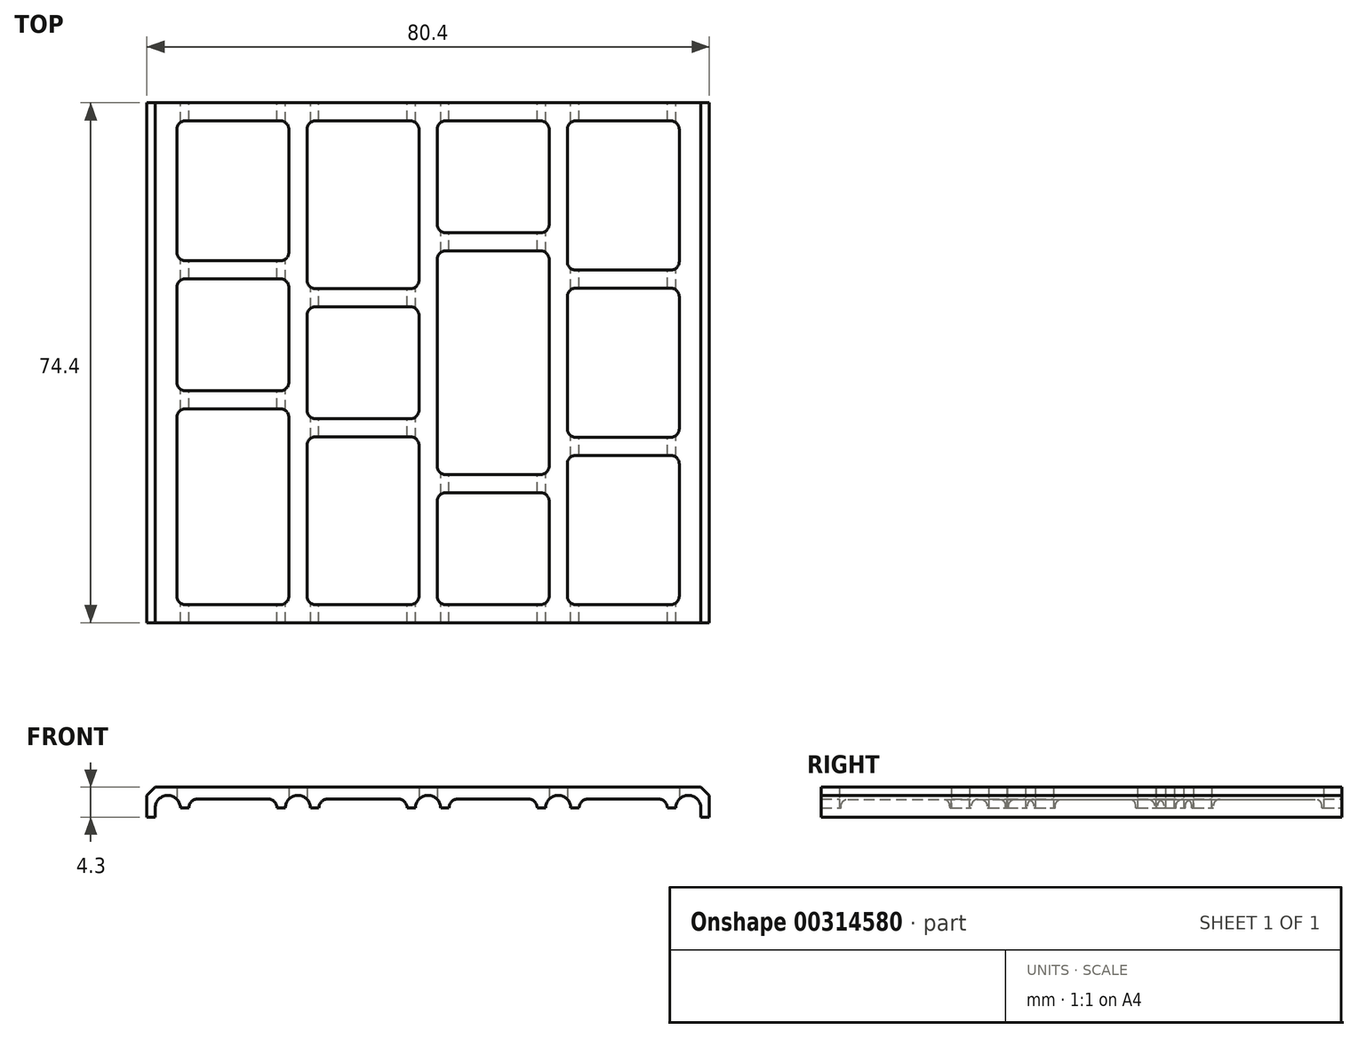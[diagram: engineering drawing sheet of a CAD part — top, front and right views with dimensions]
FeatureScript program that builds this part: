
annotation { "Feature Type Name" : "Feature", "Feature Type Description" : "" }
export const myFeature = defineFeature(function(context is Context, id is Id, definition is map)
    precondition{}
    {
        {
            var Q0;
            Q0=qCreatedBy(makeId("Front.planeOp"),FACE);
            var sketch = newSketch(context, id + "F0", { "sketchPlane" : qUnion([Q0])});
            skCircle(sketch, "E0", {"center": v(-37.2, -1.3) * mm, "radius": 1.3 * mm});
            skLineSegment(sketch, "E1", {"start": v(-37.2, -1.3) * mm, "end": v(-37.2, 0) * mm, "construction": true});
            skLineSegment(sketch, "E2", {"start": v(0, 0) * mm, "end": v(0, -7.18) * mm, "construction": true});
            skPoint(sketch, "E3", {"position": v(-38.5, -1.3) * mm});
            skCircle(sketch, "E4.1.0.0", {"center": v(-18.6, -1.3) * mm, "radius": 1.3 * mm});
            skCircle(sketch, "E4.2.0.0", {"center": v(0, -1.3) * mm, "radius": 1.3 * mm});
            skCircle(sketch, "E4.3.0.0", {"center": v(18.6, -1.3) * mm, "radius": 1.3 * mm});
            skCircle(sketch, "E4.4.0.0", {"center": v(37.2, -1.3) * mm, "radius": 1.3 * mm});
            skLineSegment(sketch, "E4.direction1", {"start": v(-37.2, -1.3) * mm, "end": v(-18.6, -1.3) * mm, "construction": true});
            skPoint(sketch, "E5", {"position": v(38.5, -1.3) * mm});
            skLineSegment(sketch, "E6", {"start": v(37.2, -1.3) * mm, "end": v(37.2, 0) * mm, "construction": true});
            skLineSegment(sketch, "E7", {"start": v(-37.2, 0) * mm, "end": v(37.2, 0) * mm, "construction": true});
            skPoint(sketch, "E8", {"position": v(-35.9, -1.3) * mm});
            skSolve(sketch);
        }
        {
            var Q0;
            Q0=qCreatedBy(makeId("Front.planeOp"),FACE);
            var sketch = newSketch(context, id + "F1", { "sketchPlane" : qUnion([Q0])});
            skArc(sketch, "E9", {"start": v(-35.4, -1.3) * mm, "mid": v(-37.2, 0.5) * mm, "end": v(-39, -1.3) * mm});
            skArc(sketch, "E10", {"start": v(-16.8, -1.3) * mm, "mid": v(-18.6, 0.5) * mm, "end": v(-20.4, -1.3) * mm});
            skArc(sketch, "E11", {"start": v(0, 0.5) * mm, "mid": v(-1.27, -0.03) * mm, "end": v(-1.8, -1.3) * mm});
            skLineSegment(sketch, "E12.trimOffspring", {"start": v(0, 0.5) * mm, "end": v(0, 1.7) * mm});
            skLineSegment(sketch, "E13.trimOffspring", {"start": v(-16.8, -1.3) * mm, "end": v(-15.6, -1.3) * mm});
            skLineSegment(sketch, "E14.trimOffspring", {"start": v(-35.4, -1.3) * mm, "end": v(-34.2, -1.3) * mm});
            skLineSegment(sketch, "E15", {"start": v(-39, -1.3) * mm, "end": v(-39, -2.6) * mm});
            skLineSegment(sketch, "E16", {"start": v(-39, -2.6) * mm, "end": v(-40.2, -2.6) * mm});
            skLineSegment(sketch, "E17", {"start": v(-40.2, -2.6) * mm, "end": v(-40.2, 1.7) * mm});
            skLineSegment(sketch, "E18", {"start": v(-40.2, 1.7) * mm, "end": v(0, 1.7) * mm});
            skPoint(sketch, "E19", {"position": v(0, -2.6) * mm});
            skLineSegment(sketch, "E20", {"start": v(-34.2, -1.3) * mm, "end": v(-34.2, 0) * mm});
            skLineSegment(sketch, "E21", {"start": v(-34.2, 0) * mm, "end": v(-21.6, 0) * mm});
            skLineSegment(sketch, "E22", {"start": v(-21.6, 0) * mm, "end": v(-21.6, -1.3) * mm});
            skLineSegment(sketch, "E23", {"start": v(-15.6, -1.3) * mm, "end": v(-15.6, 0) * mm});
            skLineSegment(sketch, "E24", {"start": v(-15.6, 0) * mm, "end": v(-3, 0) * mm});
            skLineSegment(sketch, "E25", {"start": v(-3, 0) * mm, "end": v(-3, -1.3) * mm});
            skLineSegment(sketch, "E26.trimOffspring", {"start": v(-21.6, -1.3) * mm, "end": v(-20.4, -1.3) * mm});
            skLineSegment(sketch, "E27.trimOffspring", {"start": v(-3, -1.3) * mm, "end": v(-1.8, -1.3) * mm});
            skSolve(sketch);
        }
        {
            var Q0;
            Q0 = qSketchRegion(id + "F1", true);
            extrude(context, id + "F2", {"entities" : qUnion([Q0]), "depth" : (77 - 5.2 + 2.6) * mm});
        }
        {
            var Q0;
            Q0=makeQuery(id+"F2.opExtrude","SWEPT_EDGE",EDGE,{"disambiguationData":[OSD([sQuery(id+"F1.wireOp",EDGE,"E20"),sQuery(id+"F1.wireOp",EDGE,"E21")])]});
            var Q1;
            Q1=makeQuery(id+"F2.opExtrude","SWEPT_EDGE",EDGE,{"disambiguationData":[OSD([sQuery(id+"F1.wireOp",EDGE,"E21"),sQuery(id+"F1.wireOp",EDGE,"E22")])]});
            var Q2;
            Q2=makeQuery(id+"F2.opExtrude","SWEPT_EDGE",EDGE,{"disambiguationData":[OSD([sQuery(id+"F1.wireOp",EDGE,"E23"),sQuery(id+"F1.wireOp",EDGE,"E24")])]});
            var Q3;
            Q3=makeQuery(id+"F2.opExtrude","SWEPT_EDGE",EDGE,{"disambiguationData":[OSD([sQuery(id+"F1.wireOp",EDGE,"E24"),sQuery(id+"F1.wireOp",EDGE,"E25")])]});
            fillet(context, id + "F3", {"entities" : qUnion([Q0, Q1, Q2, Q3]), "radius" : 1.3 * mm, "tangentPropagation" : true, "allowEdgeOverflow" : false});
        }
        {
            var Q0;
            Q0=makeQuery(id+"F2.opExtrude","SWEPT_EDGE",EDGE,{"disambiguationData":[OSD([sQuery(id+"F1.wireOp",EDGE,"E17"),sQuery(id+"F1.wireOp",EDGE,"E18")])]});
            chamfer(context, id + "F4", {"entities" : qUnion([Q0]), "width" : 1.2 * mm, "tangentPropagation" : true});
        }
        {
            var Q0;
            Q0=makeQuery(id+"F2.opExtrude","SWEPT_BODY",BODY,{"disambiguationData":[OSD([sQuery(id+"F1.wireOp",EDGE,"E9"),sQuery(id+"F1.wireOp",EDGE,"E10"),sQuery(id+"F1.wireOp",EDGE,"E11"),sQuery(id+"F1.wireOp",EDGE,"E12.trimOffspring"),sQuery(id+"F1.wireOp",EDGE,"E13.trimOffspring"),sQuery(id+"F1.wireOp",EDGE,"E14.trimOffspring"),sQuery(id+"F1.wireOp",EDGE,"E15"),sQuery(id+"F1.wireOp",EDGE,"E16"),sQuery(id+"F1.wireOp",EDGE,"E17"),sQuery(id+"F1.wireOp",EDGE,"E18"),sQuery(id+"F1.wireOp",EDGE,"E20"),sQuery(id+"F1.wireOp",EDGE,"E21"),sQuery(id+"F1.wireOp",EDGE,"E22"),sQuery(id+"F1.wireOp",EDGE,"E23"),sQuery(id+"F1.wireOp",EDGE,"E24"),sQuery(id+"F1.wireOp",EDGE,"E25"),sQuery(id+"F1.wireOp",EDGE,"E26.trimOffspring"),sQuery(id+"F1.wireOp",EDGE,"E27.trimOffspring")])]});
            var Q1;
            Q1=qCreatedBy(makeId("Right.planeOp"),FACE);
            mirror(context, id + "F5", {"operationType" : NewBodyOperationType.ADD, "entities" : qUnion([Q0]), "mirrorPlane" : qUnion([Q1])});
        }
        {
            var Q0;
            Q0=qCreatedBy(makeId("Top.planeOp"),FACE);
            var sketch = newSketch(context, id + "F6", { "sketchPlane" : qUnion([Q0])});
            skLineSegment(sketch, "E28.bottom", {"start": v(-35.9, -2.6) * mm, "end": v(-19.9, -2.6) * mm});
            skLineSegment(sketch, "E28.top", {"start": v(-35.9, -22.6) * mm, "end": v(-19.9, -22.6) * mm});
            skLineSegment(sketch, "E28.left", {"start": v(-35.9, -2.6) * mm, "end": v(-35.9, -22.6) * mm});
            skLineSegment(sketch, "E29", {"start": v(-19.9, -2.6) * mm, "end": v(-19.9, -22.6) * mm});
            skLineSegment(sketch, "E30.bottom", {"start": v(-35.9, -25.2) * mm, "end": v(-19.9, -25.2) * mm});
            skLineSegment(sketch, "E30.top", {"start": v(-35.9, -41.2) * mm, "end": v(-19.9, -41.2) * mm});
            skLineSegment(sketch, "E30.left", {"start": v(-35.9, -25.2) * mm, "end": v(-35.9, -41.2) * mm});
            skLineSegment(sketch, "E30.right", {"start": v(-19.9, -25.2) * mm, "end": v(-19.9, -41.2) * mm});
            skLineSegment(sketch, "E31.bottom", {"start": v(-35.9, -43.8) * mm, "end": v(-19.9, -43.8) * mm});
            skLineSegment(sketch, "E31.top", {"start": v(-35.9, -71.8) * mm, "end": v(-19.9, -71.8) * mm});
            skLineSegment(sketch, "E31.left", {"start": v(-35.9, -43.8) * mm, "end": v(-35.9, -71.8) * mm});
            skLineSegment(sketch, "E31.right", {"start": v(-19.9, -43.8) * mm, "end": v(-19.9, -71.8) * mm});
            skLineSegment(sketch, "E32.bottom", {"start": v(-17.3, -71.8) * mm, "end": v(-1.3, -71.8) * mm});
            skLineSegment(sketch, "E32.top", {"start": v(-17.3, -47.8) * mm, "end": v(-1.3, -47.8) * mm});
            skLineSegment(sketch, "E32.left", {"start": v(-17.3, -71.8) * mm, "end": v(-17.3, -47.8) * mm});
            skLineSegment(sketch, "E32.right", {"start": v(-1.3, -71.8) * mm, "end": v(-1.3, -47.8) * mm});
            skLineSegment(sketch, "E33.bottom", {"start": v(1.3, -71.8) * mm, "end": v(17.3, -71.8) * mm});
            skLineSegment(sketch, "E33.top", {"start": v(1.3, -55.8) * mm, "end": v(17.3, -55.8) * mm});
            skLineSegment(sketch, "E33.left", {"start": v(1.3, -71.8) * mm, "end": v(1.3, -55.8) * mm});
            skLineSegment(sketch, "E33.right", {"start": v(17.3, -71.8) * mm, "end": v(17.3, -55.8) * mm});
            skLineSegment(sketch, "E34.bottom", {"start": v(-17.3, -45.2) * mm, "end": v(-1.3, -45.2) * mm});
            skLineSegment(sketch, "E34.top", {"start": v(-17.3, -29.2) * mm, "end": v(-1.3, -29.2) * mm});
            skLineSegment(sketch, "E34.left", {"start": v(-17.3, -45.2) * mm, "end": v(-17.3, -29.2) * mm});
            skLineSegment(sketch, "E34.right", {"start": v(-1.3, -45.2) * mm, "end": v(-1.3, -29.2) * mm});
            skLineSegment(sketch, "E35.bottom", {"start": v(-17.3, -26.6) * mm, "end": v(-1.3, -26.6) * mm});
            skLineSegment(sketch, "E35.top", {"start": v(-17.3, -2.6) * mm, "end": v(-1.3, -2.6) * mm});
            skLineSegment(sketch, "E35.left", {"start": v(-17.3, -26.6) * mm, "end": v(-17.3, -2.6) * mm});
            skLineSegment(sketch, "E35.right", {"start": v(-1.3, -26.6) * mm, "end": v(-1.3, -2.6) * mm});
            skLineSegment(sketch, "E36.bottom", {"start": v(1.3, -2.6) * mm, "end": v(17.3, -2.6) * mm});
            skLineSegment(sketch, "E36.top", {"start": v(1.3, -18.6) * mm, "end": v(17.3, -18.6) * mm});
            skLineSegment(sketch, "E36.left", {"start": v(1.3, -2.6) * mm, "end": v(1.3, -18.6) * mm});
            skLineSegment(sketch, "E36.right", {"start": v(17.3, -2.6) * mm, "end": v(17.3, -18.6) * mm});
            skLineSegment(sketch, "E37.bottom", {"start": v(1.3, -21.2) * mm, "end": v(17.3, -21.2) * mm});
            skLineSegment(sketch, "E37.top", {"start": v(1.3, -53.2) * mm, "end": v(17.3, -53.2) * mm});
            skLineSegment(sketch, "E37.left", {"start": v(1.3, -21.2) * mm, "end": v(1.3, -53.2) * mm});
            skLineSegment(sketch, "E37.right", {"start": v(17.3, -21.2) * mm, "end": v(17.3, -53.2) * mm});
            skLineSegment(sketch, "E38.bottom", {"start": v(19.9, -2.6) * mm, "end": v(35.9, -2.6) * mm});
            skLineSegment(sketch, "E38.top", {"start": v(19.9, -71.8) * mm, "end": v(35.9, -71.8) * mm});
            skLineSegment(sketch, "E38.left", {"start": v(19.9, -2.6) * mm, "end": v(19.9, -23.93) * mm});
            skLineSegment(sketch, "E38.right", {"start": v(35.9, -2.6) * mm, "end": v(35.9, -23.93) * mm});
            skLineSegment(sketch, "E39", {"start": v(19.9, -23.93) * mm, "end": v(35.9, -23.93) * mm});
            skLineSegment(sketch, "E40", {"start": v(19.9, -26.53) * mm, "end": v(35.9, -26.53) * mm});
            skLineSegment(sketch, "E41.trimOffspring", {"start": v(19.9, -26.53) * mm, "end": v(19.9, -47.87) * mm});
            skLineSegment(sketch, "E42.trimOffspring", {"start": v(35.9, -26.53) * mm, "end": v(35.9, -47.87) * mm});
            skLineSegment(sketch, "E43", {"start": v(19.9, -47.87) * mm, "end": v(35.9, -47.87) * mm});
            skLineSegment(sketch, "E44", {"start": v(35.9, -50.47) * mm, "end": v(19.9, -50.47) * mm});
            skLineSegment(sketch, "E45.trimOffspring", {"start": v(19.9, -50.47) * mm, "end": v(19.9, -71.8) * mm});
            skLineSegment(sketch, "E46.trimOffspring", {"start": v(35.9, -50.47) * mm, "end": v(35.9, -71.8) * mm});
            skSolve(sketch);
        }
        {
            var Q0;
            Q0 = qSketchRegion(id + "F6", true);
            extrude(context, id + "F7", {"entities" : qUnion([Q0]), "operationType" : NewBodyOperationType.REMOVE, "endBound" : BoundingType.THROUGH_ALL, "depth" : 25 * mm, "hasSecondDirection" : true, "secondDirectionBound" : SecondDirectionBoundingType.THROUGH_ALL, "secondDirectionOppositeDirection" : true, "secondDirectionDepth" : 25 * mm});
        }
        {
            var Q0;
            Q0=makeQuery(id+"F7.boolean.opBoolean","COPY",EDGE,{"derivedFrom":makeQuery(id+"F7.opExtrude","SWEPT_EDGE",EDGE,{"disambiguationData":[OSD([sQuery(id+"F6.wireOp",EDGE,"E28.bottom"),sQuery(id+"F6.wireOp",EDGE,"E29")])]})});
            var Q1;
            Q1=makeQuery(id+"F7.boolean.opBoolean","COPY",EDGE,{"derivedFrom":makeQuery(id+"F7.opExtrude","SWEPT_EDGE",EDGE,{"disambiguationData":[OSD([sQuery(id+"F6.wireOp",EDGE,"E28.bottom"),sQuery(id+"F6.wireOp",EDGE,"E28.left")])]})});
            var Q2;
            Q2=makeQuery(id+"F7.boolean.opBoolean","COPY",EDGE,{"derivedFrom":makeQuery(id+"F7.opExtrude","SWEPT_EDGE",EDGE,{"disambiguationData":[OSD([sQuery(id+"F6.wireOp",EDGE,"E28.top"),sQuery(id+"F6.wireOp",EDGE,"E29")])]})});
            var Q3;
            Q3=makeQuery(id+"F7.boolean.opBoolean","COPY",EDGE,{"derivedFrom":makeQuery(id+"F7.opExtrude","SWEPT_EDGE",EDGE,{"disambiguationData":[OSD([sQuery(id+"F6.wireOp",EDGE,"E28.top"),sQuery(id+"F6.wireOp",EDGE,"E28.left")])]})});
            var Q4;
            Q4=makeQuery(id+"F7.boolean.opBoolean","COPY",EDGE,{"derivedFrom":makeQuery(id+"F7.opExtrude","SWEPT_EDGE",EDGE,{"disambiguationData":[OSD([sQuery(id+"F6.wireOp",EDGE,"E30.bottom"),sQuery(id+"F6.wireOp",EDGE,"E30.left")])]})});
            var Q5;
            Q5=makeQuery(id+"F7.boolean.opBoolean","COPY",EDGE,{"derivedFrom":makeQuery(id+"F7.opExtrude","SWEPT_EDGE",EDGE,{"disambiguationData":[OSD([sQuery(id+"F6.wireOp",EDGE,"E30.top"),sQuery(id+"F6.wireOp",EDGE,"E30.left")])]})});
            var Q6;
            Q6=makeQuery(id+"F7.boolean.opBoolean","COPY",EDGE,{"derivedFrom":makeQuery(id+"F7.opExtrude","SWEPT_EDGE",EDGE,{"disambiguationData":[OSD([sQuery(id+"F6.wireOp",EDGE,"E31.top"),sQuery(id+"F6.wireOp",EDGE,"E31.left")])]})});
            var Q7;
            Q7=makeQuery(id+"F7.boolean.opBoolean","COPY",EDGE,{"derivedFrom":makeQuery(id+"F7.opExtrude","SWEPT_EDGE",EDGE,{"disambiguationData":[OSD([sQuery(id+"F6.wireOp",EDGE,"E31.bottom"),sQuery(id+"F6.wireOp",EDGE,"E31.left")])]})});
            var Q8;
            Q8=makeQuery(id+"F7.boolean.opBoolean","COPY",EDGE,{"derivedFrom":makeQuery(id+"F7.opExtrude","SWEPT_EDGE",EDGE,{"disambiguationData":[OSD([sQuery(id+"F6.wireOp",EDGE,"E30.bottom"),sQuery(id+"F6.wireOp",EDGE,"E30.right")])]})});
            var Q9;
            Q9=makeQuery(id+"F7.boolean.opBoolean","COPY",EDGE,{"derivedFrom":makeQuery(id+"F7.opExtrude","SWEPT_EDGE",EDGE,{"disambiguationData":[OSD([sQuery(id+"F6.wireOp",EDGE,"E30.top"),sQuery(id+"F6.wireOp",EDGE,"E30.right")])]})});
            var Q10;
            Q10=makeQuery(id+"F7.boolean.opBoolean","COPY",EDGE,{"derivedFrom":makeQuery(id+"F7.opExtrude","SWEPT_EDGE",EDGE,{"disambiguationData":[OSD([sQuery(id+"F6.wireOp",EDGE,"E31.bottom"),sQuery(id+"F6.wireOp",EDGE,"E31.right")])]})});
            var Q11;
            Q11=makeQuery(id+"F7.boolean.opBoolean","COPY",EDGE,{"derivedFrom":makeQuery(id+"F7.opExtrude","SWEPT_EDGE",EDGE,{"disambiguationData":[OSD([sQuery(id+"F6.wireOp",EDGE,"E31.top"),sQuery(id+"F6.wireOp",EDGE,"E31.right")])]})});
            var Q12;
            Q12=makeQuery(id+"F7.boolean.opBoolean","COPY",EDGE,{"derivedFrom":makeQuery(id+"F7.opExtrude","SWEPT_EDGE",EDGE,{"disambiguationData":[OSD([sQuery(id+"F6.wireOp",EDGE,"E35.bottom"),sQuery(id+"F6.wireOp",EDGE,"E35.left")])]})});
            var Q13;
            Q13=makeQuery(id+"F7.boolean.opBoolean","COPY",EDGE,{"derivedFrom":makeQuery(id+"F7.opExtrude","SWEPT_EDGE",EDGE,{"disambiguationData":[OSD([sQuery(id+"F6.wireOp",EDGE,"E34.bottom"),sQuery(id+"F6.wireOp",EDGE,"E34.left")])]})});
            var Q14;
            Q14=makeQuery(id+"F7.boolean.opBoolean","COPY",EDGE,{"derivedFrom":makeQuery(id+"F7.opExtrude","SWEPT_EDGE",EDGE,{"disambiguationData":[OSD([sQuery(id+"F6.wireOp",EDGE,"E32.bottom"),sQuery(id+"F6.wireOp",EDGE,"E32.left")])]})});
            var Q15;
            Q15=makeQuery(id+"F7.boolean.opBoolean","COPY",EDGE,{"derivedFrom":makeQuery(id+"F7.opExtrude","SWEPT_EDGE",EDGE,{"disambiguationData":[OSD([sQuery(id+"F6.wireOp",EDGE,"E35.top"),sQuery(id+"F6.wireOp",EDGE,"E35.left")])]})});
            var Q16;
            Q16=makeQuery(id+"F7.boolean.opBoolean","COPY",EDGE,{"derivedFrom":makeQuery(id+"F7.opExtrude","SWEPT_EDGE",EDGE,{"disambiguationData":[OSD([sQuery(id+"F6.wireOp",EDGE,"E34.top"),sQuery(id+"F6.wireOp",EDGE,"E34.left")])]})});
            var Q17;
            Q17=makeQuery(id+"F7.boolean.opBoolean","COPY",EDGE,{"derivedFrom":makeQuery(id+"F7.opExtrude","SWEPT_EDGE",EDGE,{"disambiguationData":[OSD([sQuery(id+"F6.wireOp",EDGE,"E35.top"),sQuery(id+"F6.wireOp",EDGE,"E35.right")])]})});
            var Q18;
            Q18=makeQuery(id+"F7.boolean.opBoolean","COPY",EDGE,{"derivedFrom":makeQuery(id+"F7.opExtrude","SWEPT_EDGE",EDGE,{"disambiguationData":[OSD([sQuery(id+"F6.wireOp",EDGE,"E34.top"),sQuery(id+"F6.wireOp",EDGE,"E34.right")])]})});
            var Q19;
            Q19=makeQuery(id+"F7.boolean.opBoolean","COPY",EDGE,{"derivedFrom":makeQuery(id+"F7.opExtrude","SWEPT_EDGE",EDGE,{"disambiguationData":[OSD([sQuery(id+"F6.wireOp",EDGE,"E32.top"),sQuery(id+"F6.wireOp",EDGE,"E32.right")])]})});
            var Q20;
            Q20=makeQuery(id+"F7.boolean.opBoolean","COPY",EDGE,{"derivedFrom":makeQuery(id+"F7.opExtrude","SWEPT_EDGE",EDGE,{"disambiguationData":[OSD([sQuery(id+"F6.wireOp",EDGE,"E32.bottom"),sQuery(id+"F6.wireOp",EDGE,"E32.right")])]})});
            var Q21;
            Q21=makeQuery(id+"F7.boolean.opBoolean","COPY",EDGE,{"derivedFrom":makeQuery(id+"F7.opExtrude","SWEPT_EDGE",EDGE,{"disambiguationData":[OSD([sQuery(id+"F6.wireOp",EDGE,"E34.bottom"),sQuery(id+"F6.wireOp",EDGE,"E34.right")])]})});
            var Q22;
            Q22=makeQuery(id+"F7.boolean.opBoolean","COPY",EDGE,{"derivedFrom":makeQuery(id+"F7.opExtrude","SWEPT_EDGE",EDGE,{"disambiguationData":[OSD([sQuery(id+"F6.wireOp",EDGE,"E35.bottom"),sQuery(id+"F6.wireOp",EDGE,"E35.right")])]})});
            var Q23;
            Q23=makeQuery(id+"F7.boolean.opBoolean","COPY",EDGE,{"derivedFrom":makeQuery(id+"F7.opExtrude","SWEPT_EDGE",EDGE,{"disambiguationData":[OSD([sQuery(id+"F6.wireOp",EDGE,"E33.bottom"),sQuery(id+"F6.wireOp",EDGE,"E33.right")])]})});
            var Q24;
            Q24=makeQuery(id+"F7.boolean.opBoolean","COPY",EDGE,{"derivedFrom":makeQuery(id+"F7.opExtrude","SWEPT_EDGE",EDGE,{"disambiguationData":[OSD([sQuery(id+"F6.wireOp",EDGE,"E37.top"),sQuery(id+"F6.wireOp",EDGE,"E37.right")])]})});
            var Q25;
            Q25=makeQuery(id+"F7.boolean.opBoolean","COPY",EDGE,{"derivedFrom":makeQuery(id+"F7.opExtrude","SWEPT_EDGE",EDGE,{"disambiguationData":[OSD([sQuery(id+"F6.wireOp",EDGE,"E36.top"),sQuery(id+"F6.wireOp",EDGE,"E36.right")])]})});
            var Q26;
            Q26=makeQuery(id+"F7.boolean.opBoolean","COPY",EDGE,{"derivedFrom":makeQuery(id+"F7.opExtrude","SWEPT_EDGE",EDGE,{"disambiguationData":[OSD([sQuery(id+"F6.wireOp",EDGE,"E38.right"),sQuery(id+"F6.wireOp",EDGE,"E39")])]})});
            var Q27;
            Q27=makeQuery(id+"F7.boolean.opBoolean","COPY",EDGE,{"derivedFrom":makeQuery(id+"F7.opExtrude","SWEPT_EDGE",EDGE,{"disambiguationData":[OSD([sQuery(id+"F6.wireOp",EDGE,"E42.trimOffspring"),sQuery(id+"F6.wireOp",EDGE,"E43")])]})});
            var Q28;
            Q28=makeQuery(id+"F7.boolean.opBoolean","COPY",EDGE,{"derivedFrom":makeQuery(id+"F7.opExtrude","SWEPT_EDGE",EDGE,{"disambiguationData":[OSD([sQuery(id+"F6.wireOp",EDGE,"E38.top"),sQuery(id+"F6.wireOp",EDGE,"E46.trimOffspring")])]})});
            var Q29;
            Q29=makeQuery(id+"F7.boolean.opBoolean","COPY",EDGE,{"derivedFrom":makeQuery(id+"F7.opExtrude","SWEPT_EDGE",EDGE,{"disambiguationData":[OSD([sQuery(id+"F6.wireOp",EDGE,"E38.bottom"),sQuery(id+"F6.wireOp",EDGE,"E38.right")])]})});
            var Q30;
            Q30=makeQuery(id+"F7.boolean.opBoolean","COPY",EDGE,{"derivedFrom":makeQuery(id+"F7.opExtrude","SWEPT_EDGE",EDGE,{"disambiguationData":[OSD([sQuery(id+"F6.wireOp",EDGE,"E36.bottom"),sQuery(id+"F6.wireOp",EDGE,"E36.right")])]})});
            var Q31;
            Q31=makeQuery(id+"F7.boolean.opBoolean","COPY",EDGE,{"derivedFrom":makeQuery(id+"F7.opExtrude","SWEPT_EDGE",EDGE,{"disambiguationData":[OSD([sQuery(id+"F6.wireOp",EDGE,"E37.bottom"),sQuery(id+"F6.wireOp",EDGE,"E37.right")])]})});
            var Q32;
            Q32=makeQuery(id+"F7.boolean.opBoolean","COPY",EDGE,{"derivedFrom":makeQuery(id+"F7.opExtrude","SWEPT_EDGE",EDGE,{"disambiguationData":[OSD([sQuery(id+"F6.wireOp",EDGE,"E33.top"),sQuery(id+"F6.wireOp",EDGE,"E33.right")])]})});
            var Q33;
            Q33=makeQuery(id+"F7.boolean.opBoolean","COPY",EDGE,{"derivedFrom":makeQuery(id+"F7.opExtrude","SWEPT_EDGE",EDGE,{"disambiguationData":[OSD([sQuery(id+"F6.wireOp",EDGE,"E38.top"),sQuery(id+"F6.wireOp",EDGE,"E45.trimOffspring")])]})});
            var Q34;
            Q34=makeQuery(id+"F7.boolean.opBoolean","COPY",EDGE,{"derivedFrom":makeQuery(id+"F7.opExtrude","SWEPT_EDGE",EDGE,{"disambiguationData":[OSD([sQuery(id+"F6.wireOp",EDGE,"E33.bottom"),sQuery(id+"F6.wireOp",EDGE,"E33.left")])]})});
            var Q35;
            Q35=makeQuery(id+"F7.boolean.opBoolean","COPY",EDGE,{"derivedFrom":makeQuery(id+"F7.opExtrude","SWEPT_EDGE",EDGE,{"disambiguationData":[OSD([sQuery(id+"F6.wireOp",EDGE,"E37.top"),sQuery(id+"F6.wireOp",EDGE,"E37.left")])]})});
            var Q36;
            Q36=makeQuery(id+"F7.boolean.opBoolean","COPY",EDGE,{"derivedFrom":makeQuery(id+"F7.opExtrude","SWEPT_EDGE",EDGE,{"disambiguationData":[OSD([sQuery(id+"F6.wireOp",EDGE,"E36.top"),sQuery(id+"F6.wireOp",EDGE,"E36.left")])]})});
            var Q37;
            Q37=makeQuery(id+"F7.boolean.opBoolean","COPY",EDGE,{"derivedFrom":makeQuery(id+"F7.opExtrude","SWEPT_EDGE",EDGE,{"disambiguationData":[OSD([sQuery(id+"F6.wireOp",EDGE,"E41.trimOffspring"),sQuery(id+"F6.wireOp",EDGE,"E43")])]})});
            var Q38;
            Q38=makeQuery(id+"F7.boolean.opBoolean","COPY",EDGE,{"derivedFrom":makeQuery(id+"F7.opExtrude","SWEPT_EDGE",EDGE,{"disambiguationData":[OSD([sQuery(id+"F6.wireOp",EDGE,"E38.left"),sQuery(id+"F6.wireOp",EDGE,"E39")])]})});
            var Q39;
            Q39=makeQuery(id+"F7.boolean.opBoolean","COPY",EDGE,{"derivedFrom":makeQuery(id+"F7.opExtrude","SWEPT_EDGE",EDGE,{"disambiguationData":[OSD([sQuery(id+"F6.wireOp",EDGE,"E33.top"),sQuery(id+"F6.wireOp",EDGE,"E33.left")])]})});
            var Q40;
            Q40=makeQuery(id+"F7.boolean.opBoolean","COPY",EDGE,{"derivedFrom":makeQuery(id+"F7.opExtrude","SWEPT_EDGE",EDGE,{"disambiguationData":[OSD([sQuery(id+"F6.wireOp",EDGE,"E44"),sQuery(id+"F6.wireOp",EDGE,"E45.trimOffspring")])]})});
            var Q41;
            Q41=makeQuery(id+"F7.boolean.opBoolean","COPY",EDGE,{"derivedFrom":makeQuery(id+"F7.opExtrude","SWEPT_EDGE",EDGE,{"disambiguationData":[OSD([sQuery(id+"F6.wireOp",EDGE,"E37.bottom"),sQuery(id+"F6.wireOp",EDGE,"E37.left")])]})});
            var Q42;
            Q42=makeQuery(id+"F7.boolean.opBoolean","COPY",EDGE,{"derivedFrom":makeQuery(id+"F7.opExtrude","SWEPT_EDGE",EDGE,{"disambiguationData":[OSD([sQuery(id+"F6.wireOp",EDGE,"E40"),sQuery(id+"F6.wireOp",EDGE,"E41.trimOffspring")])]})});
            var Q43;
            Q43=makeQuery(id+"F7.boolean.opBoolean","COPY",EDGE,{"derivedFrom":makeQuery(id+"F7.opExtrude","SWEPT_EDGE",EDGE,{"disambiguationData":[OSD([sQuery(id+"F6.wireOp",EDGE,"E36.bottom"),sQuery(id+"F6.wireOp",EDGE,"E36.left")])]})});
            var Q44;
            Q44=makeQuery(id+"F7.boolean.opBoolean","COPY",EDGE,{"derivedFrom":makeQuery(id+"F7.opExtrude","SWEPT_EDGE",EDGE,{"disambiguationData":[OSD([sQuery(id+"F6.wireOp",EDGE,"E38.bottom"),sQuery(id+"F6.wireOp",EDGE,"E38.left")])]})});
            var Q45;
            Q45=makeQuery(id+"F7.boolean.opBoolean","COPY",EDGE,{"derivedFrom":makeQuery(id+"F7.opExtrude","SWEPT_EDGE",EDGE,{"disambiguationData":[OSD([sQuery(id+"F6.wireOp",EDGE,"E32.top"),sQuery(id+"F6.wireOp",EDGE,"E32.left")])]})});
            var Q46;
            Q46=makeQuery(id+"F7.boolean.opBoolean","COPY",EDGE,{"derivedFrom":makeQuery(id+"F7.opExtrude","SWEPT_EDGE",EDGE,{"disambiguationData":[OSD([sQuery(id+"F6.wireOp",EDGE,"E44"),sQuery(id+"F6.wireOp",EDGE,"E46.trimOffspring")])]})});
            var Q47;
            Q47=makeQuery(id+"F7.boolean.opBoolean","COPY",EDGE,{"derivedFrom":makeQuery(id+"F7.opExtrude","SWEPT_EDGE",EDGE,{"disambiguationData":[OSD([sQuery(id+"F6.wireOp",EDGE,"E40"),sQuery(id+"F6.wireOp",EDGE,"E42.trimOffspring")])]})});
            fillet(context, id + "F8", {"entities" : qUnion([Q0, Q1, Q2, Q3, Q4, Q5, Q6, Q7, Q8, Q9, Q10, Q11, Q12, Q13, Q14, Q15, Q16, Q17, Q18, Q19, Q20, Q21, Q22, Q23, Q24, Q25, Q26, Q27, Q28, Q29, Q30, Q31, Q32, Q33, Q34, Q35, Q36, Q37, Q38, Q39, Q40, Q41, Q42, Q43, Q44, Q45, Q46, Q47]), "radius" : 1.2 * mm, "tangentPropagation" : true, "allowEdgeOverflow" : false});
        }
    });
